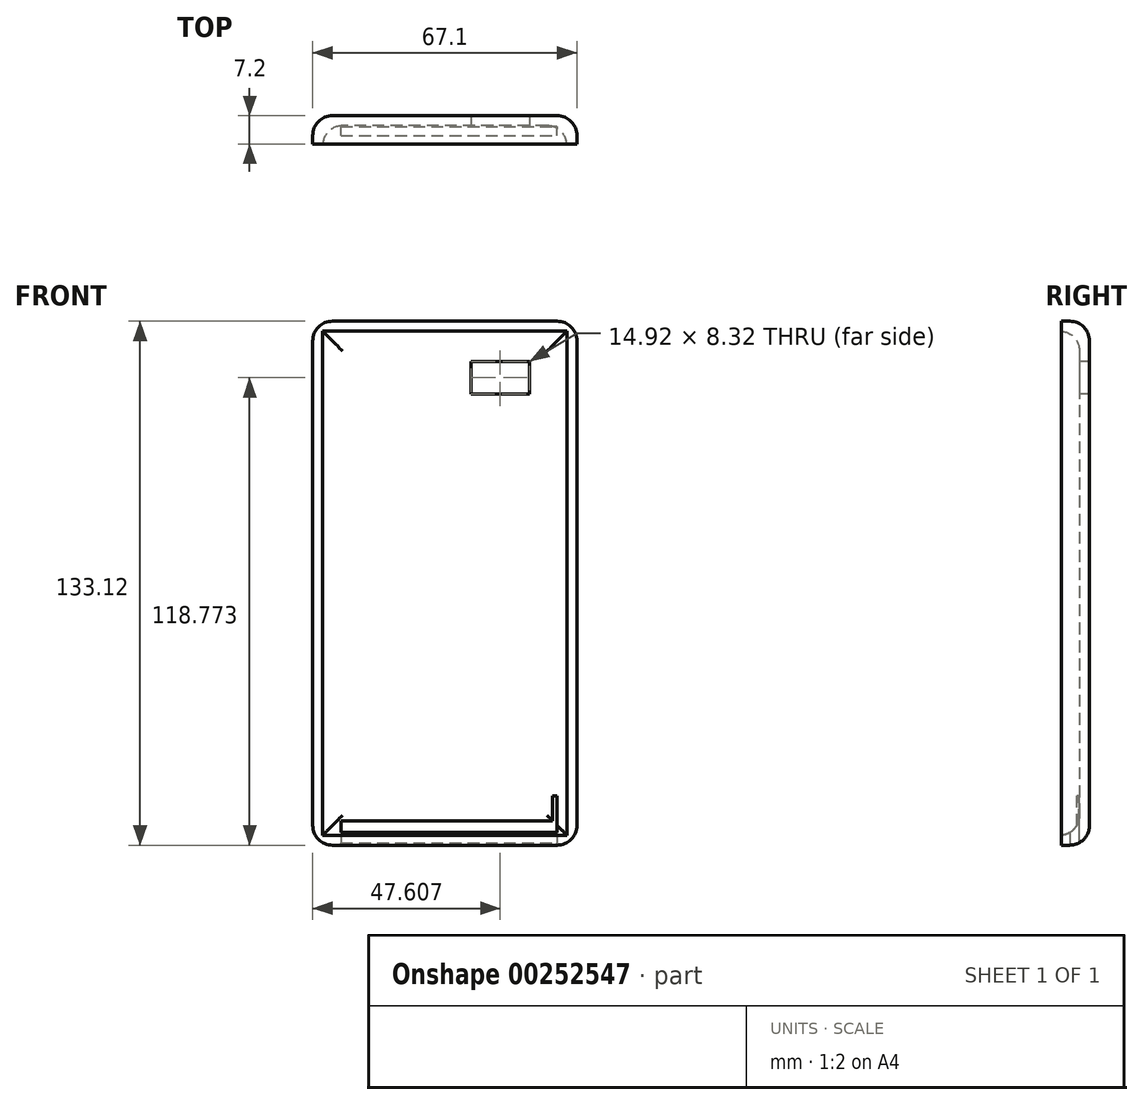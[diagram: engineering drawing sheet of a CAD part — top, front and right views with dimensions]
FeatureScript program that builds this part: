
annotation { "Feature Type Name" : "Feature", "Feature Type Description" : "" }
export const myFeature = defineFeature(function(context is Context, id is Id, definition is map)
    precondition{}
    {
        {
            var Q0;
            Q0=qCreatedBy(makeId("Front.planeOp"),FACE);
            var sketch = newSketch(context, id + "F0", { "sketchPlane" : qUnion([Q0])});
            skLineSegment(sketch, "E0.bottom", {"start": v(-33.55, -66.56) * mm, "end": v(33.55, -66.56) * mm});
            skLineSegment(sketch, "E0.top", {"start": v(-33.55, 66.56) * mm, "end": v(33.55, 66.56) * mm});
            skLineSegment(sketch, "E0.left", {"start": v(-33.55, -66.56) * mm, "end": v(-33.55, 66.56) * mm});
            skLineSegment(sketch, "E0.right", {"start": v(33.55, -66.56) * mm, "end": v(33.55, 66.56) * mm});
            skPoint(sketch, "E0.middle", {"position": v(0, 0) * mm});
            skSolve(sketch);
        }
        {
            var Q0;
            Q0=makeQuery(id+"F0.imprint","IMPRINT",FACE,{"disambiguationData":[TD([[makeQuery(id+"F0.imprint","IMPRINT",EDGE,{"derivedFrom":sQuery(id+"F0.wireOp",EDGE,"E0.bottom")}),1.0]])]});
            extrude(context, id + "F1", {"entities" : qUnion([Q0]), "depth" : 7.2 * mm});
        }
        {
            var Q0;
            Q0=makeQuery(id+"F1.opExtrude","CAP_FACE",FACE,{"disambiguationData":[OSD([sQuery(id+"F0.wireOp",EDGE,"E0.bottom"),sQuery(id+"F0.wireOp",EDGE,"E0.top"),sQuery(id+"F0.wireOp",EDGE,"E0.left"),sQuery(id+"F0.wireOp",EDGE,"E0.right")])],"isStart":false});
            shell(context, id + "F2", {"entities" : qUnion([Q0]), "thickness" : 2.54 * mm});
        }
        {
            var Q0;
            Q0=makeQuery(id+"F2.opShell","OFFSET_FACE",FACE,{"disambiguationData":[OSD([sQuery(id+"F0.wireOp",EDGE,"E0.bottom"),sQuery(id+"F0.wireOp",EDGE,"E0.top"),sQuery(id+"F0.wireOp",EDGE,"E0.left"),sQuery(id+"F0.wireOp",EDGE,"E0.right")])]});
            var Q1;
            Q1=makeQuery(id+"F1.opExtrude","CAP_FACE",FACE,{"disambiguationData":[OSD([sQuery(id+"F0.wireOp",EDGE,"E0.bottom"),sQuery(id+"F0.wireOp",EDGE,"E0.top"),sQuery(id+"F0.wireOp",EDGE,"E0.left"),sQuery(id+"F0.wireOp",EDGE,"E0.right")])],"isStart":true});
            var Q2;
            Q2=makeQuery(id+"F1.opExtrude","SWEPT_EDGE",EDGE,{"disambiguationData":[OSD([sQuery(id+"F0.wireOp",EDGE,"E0.top"),sQuery(id+"F0.wireOp",EDGE,"E0.right")])]});
            var Q3;
            Q3=makeQuery(id+"F1.opExtrude","SWEPT_EDGE",EDGE,{"disambiguationData":[OSD([sQuery(id+"F0.wireOp",EDGE,"E0.top"),sQuery(id+"F0.wireOp",EDGE,"E0.left")])]});
            var Q4;
            Q4=makeQuery(id+"F1.opExtrude","SWEPT_EDGE",EDGE,{"disambiguationData":[OSD([sQuery(id+"F0.wireOp",EDGE,"E0.bottom"),sQuery(id+"F0.wireOp",EDGE,"E0.left")])]});
            var Q5;
            Q5=makeQuery(id+"F1.opExtrude","SWEPT_EDGE",EDGE,{"disambiguationData":[OSD([sQuery(id+"F0.wireOp",EDGE,"E0.bottom"),sQuery(id+"F0.wireOp",EDGE,"E0.right")])]});
            fillet(context, id + "F3", {"entities" : qUnion([Q0, Q1, Q2, Q3, Q4, Q5]), "radius" : 5 * mm, "tangentPropagation" : true, "allowEdgeOverflow" : false});
        }
        {
            var Q0;
            Q0=makeQuery(id+"F2.opShell","OFFSET_FACE",FACE,{"disambiguationData":[OSD([sQuery(id+"F0.wireOp",EDGE,"E0.bottom"),sQuery(id+"F0.wireOp",EDGE,"E0.top"),sQuery(id+"F0.wireOp",EDGE,"E0.left"),sQuery(id+"F0.wireOp",EDGE,"E0.right")])]});
            var sketch = newSketch(context, id + "F4", { "sketchPlane" : qUnion([Q0])});
            skLineSegment(sketch, "E1.bottom", {"start": v(21.52, 56.37) * mm, "end": v(6.6, 56.37) * mm});
            skLineSegment(sketch, "E1.top", {"start": v(21.52, 48.05) * mm, "end": v(6.6, 48.05) * mm});
            skLineSegment(sketch, "E1.left", {"start": v(21.52, 56.37) * mm, "end": v(21.52, 48.05) * mm});
            skLineSegment(sketch, "E1.right", {"start": v(6.6, 56.37) * mm, "end": v(6.6, 48.05) * mm});
            skSolve(sketch);
        }
        {
            var Q0;
            Q0=makeQuery(id+"F4.imprint","IMPRINT",FACE,{"disambiguationData":[TD([[makeQuery(id+"F4.imprint","IMPRINT",EDGE,{"derivedFrom":sQuery(id+"F4.wireOp",EDGE,"E1.bottom")}),1.0]])]});
            extrude(context, id + "F5", {"entities" : qUnion([Q0]), "operationType" : NewBodyOperationType.REMOVE, "endBound" : BoundingType.SYMMETRIC, "oppositeDirection" : true, "depth" : 25 * mm});
        }
        {
            var Q0;
            Q0=makeQuery(id+"F1.opExtrude","SWEPT_FACE",FACE,{"disambiguationData":[OSD([sQuery(id+"F0.wireOp",EDGE,"E0.bottom")])]});
            var sketch = newSketch(context, id + "F6", { "sketchPlane" : qUnion([Q0])});
            skLineSegment(sketch, "E2.bottom", {"start": v(28.55, 2.73) * mm, "end": v(-26.4, 2.73) * mm});
            skLineSegment(sketch, "E2.top", {"start": v(28.55, 5) * mm, "end": v(-26.4, 5) * mm});
            skLineSegment(sketch, "E2.left", {"start": v(28.55, 2.73) * mm, "end": v(28.55, 5) * mm});
            skLineSegment(sketch, "E2.right", {"start": v(-26.4, 2.73) * mm, "end": v(-26.4, 5) * mm});
            skSolve(sketch);
        }
        {
            var Q0;
            Q0 = qSketchRegion(id + "F6", true);
            extrude(context, id + "F7", {"entities" : qUnion([Q0]), "operationType" : NewBodyOperationType.REMOVE, "endBound" : BoundingType.SYMMETRIC, "oppositeDirection" : true, "depth" : 25 * mm});
        }
    });
